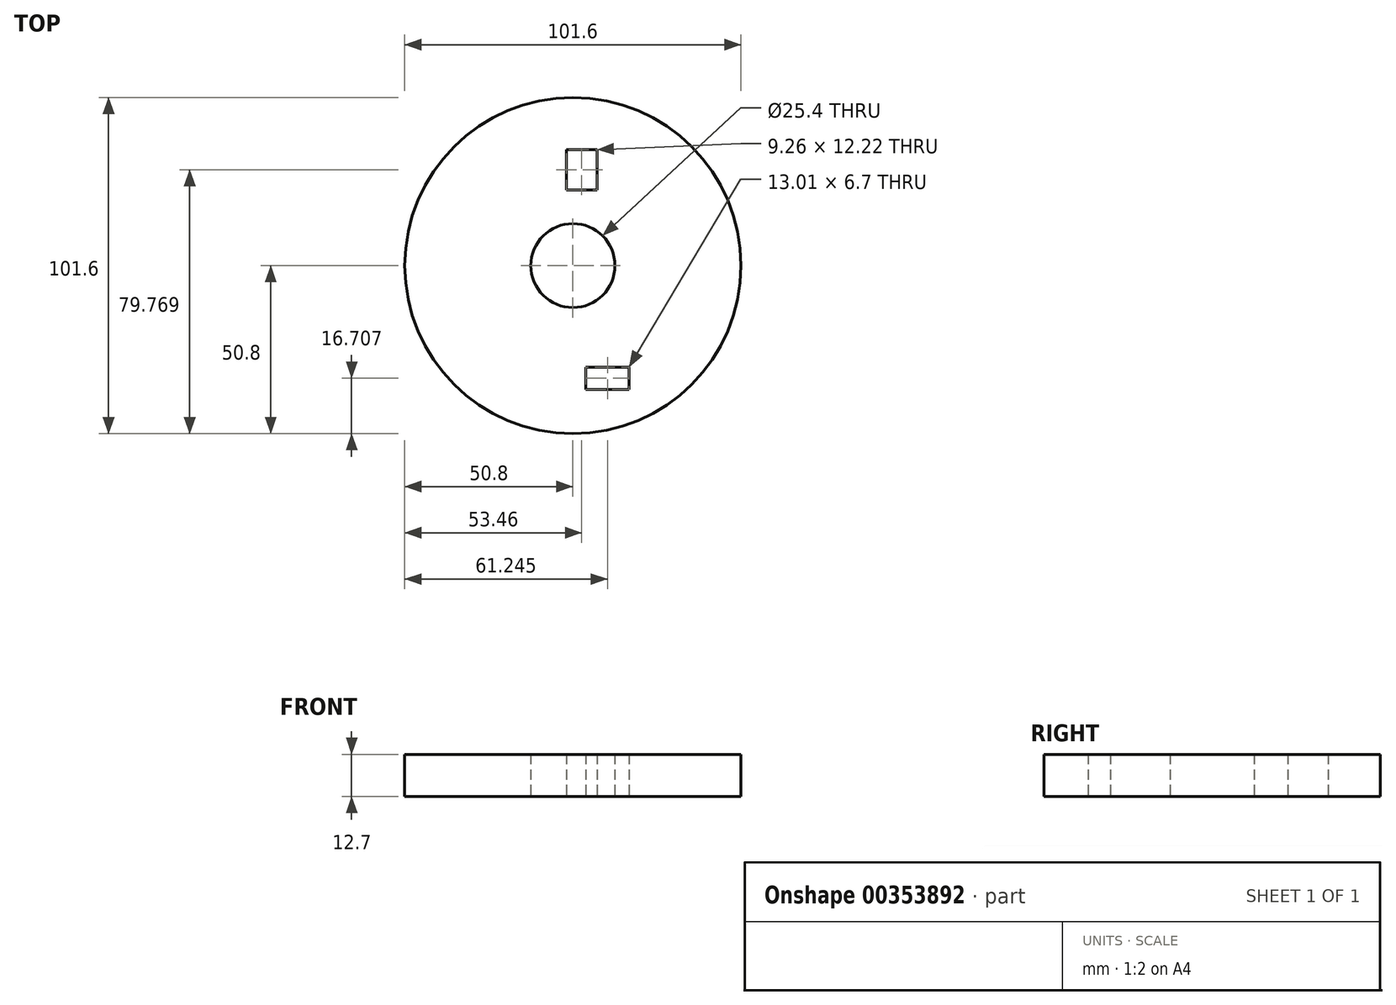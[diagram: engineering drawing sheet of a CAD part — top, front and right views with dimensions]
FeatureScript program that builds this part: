
annotation { "Feature Type Name" : "Feature", "Feature Type Description" : "" }
export const myFeature = defineFeature(function(context is Context, id is Id, definition is map)
    precondition{}
    {
        {
            var Q0;
            Q0=qCreatedBy(makeId("Top.planeOp"),FACE);
            var sketch = newSketch(context, id + "F0", { "sketchPlane" : qUnion([Q0])});
            skCircle(sketch, "E0", {"center": v(0, 0) * mm, "radius": 50.8 * mm});
            skCircle(sketch, "E1", {"center": v(0, 0) * mm, "radius": 12.7 * mm});
            skLineSegment(sketch, "E2.bottom", {"start": v(-1.97, 35.08) * mm, "end": v(7.3, 35.08) * mm});
            skLineSegment(sketch, "E2.top", {"start": v(-1.97, 22.86) * mm, "end": v(7.3, 22.86) * mm});
            skLineSegment(sketch, "E2.left", {"start": v(-1.97, 35.08) * mm, "end": v(-1.97, 22.86) * mm});
            skLineSegment(sketch, "E2.right", {"start": v(7.3, 35.08) * mm, "end": v(7.3, 22.86) * mm});
            skLineSegment(sketch, "E3.bottom", {"start": v(3.94, -30.74) * mm, "end": v(16.95, -30.74) * mm});
            skLineSegment(sketch, "E3.top", {"start": v(3.94, -37.44) * mm, "end": v(16.95, -37.44) * mm});
            skLineSegment(sketch, "E3.left", {"start": v(3.94, -30.74) * mm, "end": v(3.94, -37.44) * mm});
            skLineSegment(sketch, "E3.right", {"start": v(16.95, -30.74) * mm, "end": v(16.95, -37.44) * mm});
            skSolve(sketch);
        }
        {
            var Q0;
            Q0 = qSketchRegion(id + "F0", true);
            extrude(context, id + "F1", {"entities" : qUnion([Q0]), "endBound" : BoundingType.SYMMETRIC, "depth" : 12.7 * mm});
        }
    });
